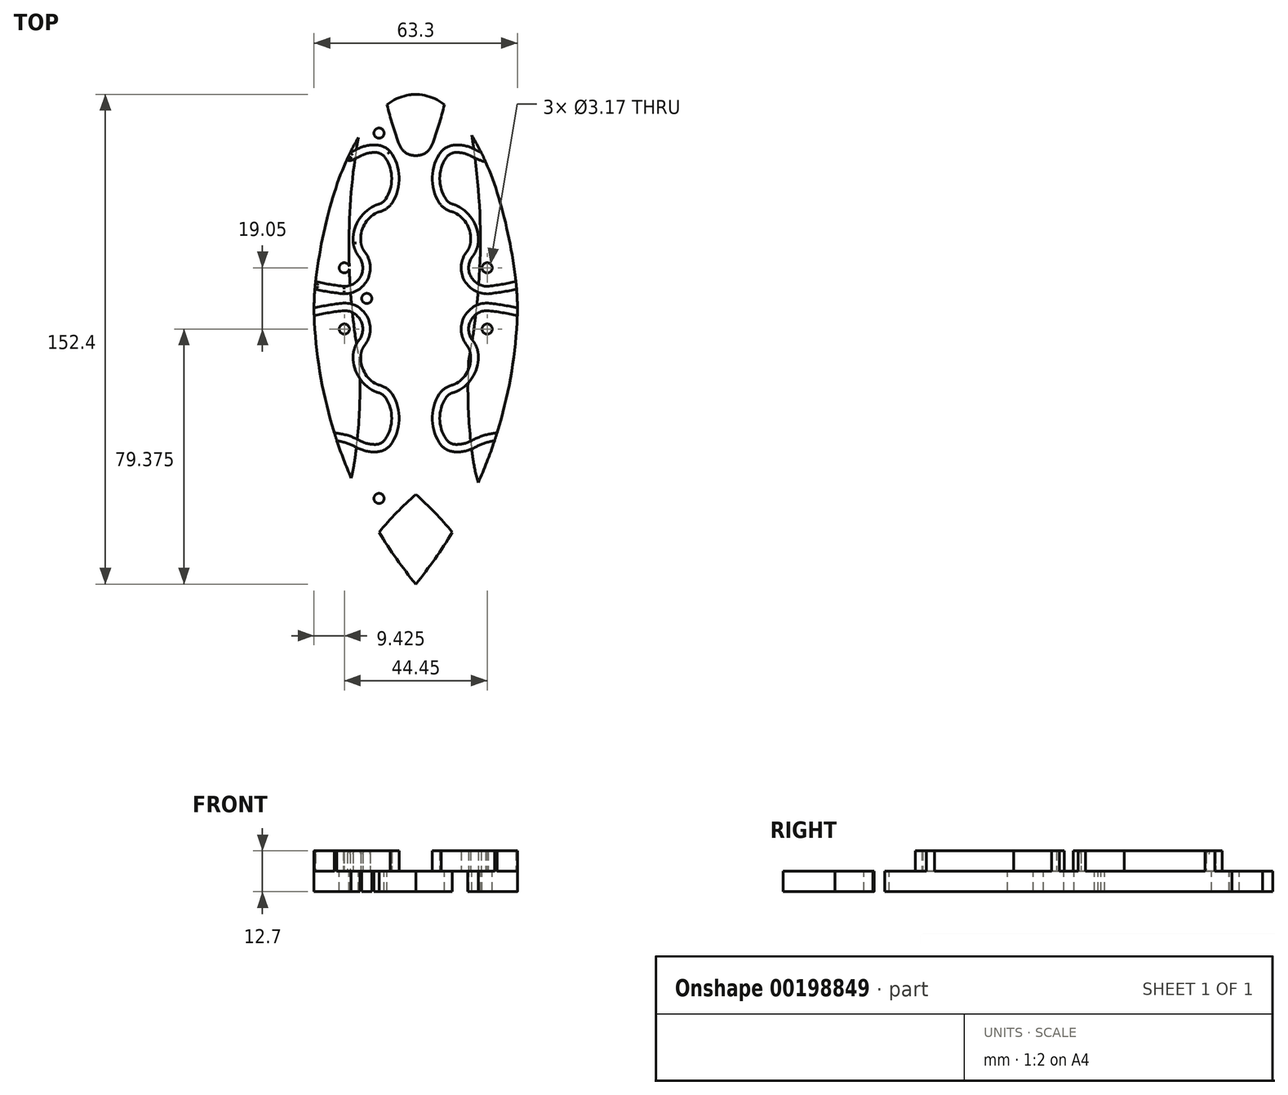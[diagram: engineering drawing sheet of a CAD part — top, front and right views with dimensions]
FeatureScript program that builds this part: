
annotation { "Feature Type Name" : "Feature", "Feature Type Description" : "" }
export const myFeature = defineFeature(function(context is Context, id is Id, definition is map)
    precondition{}
    {
        {
            var Q0;
            Q0=qCreatedBy(makeId("Top.planeOp"),FACE);
            var sketch = newSketch(context, id + "F0", { "sketchPlane" : qUnion([Q0])});
            skLineSegment(sketch, "E0", {"start": v(0, 0) * mm, "end": v(0, 80.69) * mm, "construction": true});
            skLineSegment(sketch, "E1", {"start": v(-64.8, 0) * mm, "end": v(76.72, 0) * mm, "construction": true});
            skLineSegment(sketch, "E2", {"start": v(0, 0) * mm, "end": v(0, -115.81) * mm, "construction": true});
            skPoint(sketch, "E3", {"position": v(0, 63.5) * mm});
            skPoint(sketch, "E4", {"position": v(31.75, 0) * mm});
            skPoint(sketch, "E5", {"position": v(-31.75, 0) * mm});
            skPoint(sketch, "E6", {"position": v(0, -88.9) * mm});
            skPoint(sketch, "E7", {"position": v(0, -19.05) * mm});
            skEllipticalArc(sketch, "E8", {});
            skPoint(sketch, "E9", {"position": v(0, -63.5) * mm});
            skPoint(sketch, "E10", {"position": v(16.51, -63.5) * mm});
            skArc(sketch, "E11", {"start": v(0, -88.9) * mm, "mid": v(22.23, -50.65) * mm, "end": v(31.54, -7.4) * mm});
            skArc(sketch, "E12.MirrorCS", {"start": v(0, -88.9) * mm, "mid": v(-22.23, -50.65) * mm, "end": v(-31.54, -7.4) * mm});
            skArc(sketch, "E13.filletArc", {"start": v(-31.03, 6.47) * mm, "mid": v(-31.6, -0.45) * mm, "end": v(-31.54, -7.4) * mm});
            skArc(sketch, "E14.MirrorCS", {"start": v(31.03, 6.47) * mm, "mid": v(31.6, -0.45) * mm, "end": v(31.54, -7.4) * mm});
            skPoint(sketch, "E15", {"position": v(-19.05, 76.2) * mm});
            skPoint(sketch, "E16", {"position": v(19.05, 76.2) * mm});
            skArc(sketch, "E17", {"start": v(-19.05, 47.97) * mm, "mid": v(-17.86, 62.09) * mm, "end": v(-19.05, 76.2) * mm});
            skArc(sketch, "E18", {"start": v(-19.05, 76.2) * mm, "mid": v(-11.04, 67.58) * mm, "end": v(0, 63.5) * mm});
            skArc(sketch, "E19.MirrorCS", {"start": v(19.05, 47.97) * mm, "mid": v(17.86, 62.09) * mm, "end": v(19.05, 76.2) * mm});
            skArc(sketch, "E20.MirrorCS", {"start": v(19.05, 76.2) * mm, "mid": v(11.04, 67.58) * mm, "end": v(0, 63.5) * mm});
            const initialGuessF0  = {"E8": [0, -0.01905, 0, 1, 0.08255, 0.03263075260586246, 5.026736623577707, 1.2564486836018787]};
            skSetInitialGuess(sketch, initialGuessF0);
            skSolve(sketch);
        }
        {
            var Q0;
            Q0=makeQuery(id+"F0.imprint","IMPRINT",FACE,{"disambiguationData":[TD([[makeQuery(id+"F0.imprint","IMPRINT",EDGE,{"derivedFrom":sQuery(id+"F0.wireOp",EDGE,"E8")}),1.0]])]});
            extrude(context, id + "F1", {"entities" : qUnion([Q0]), "oppositeDirection" : true, "depth" : 6.35 * mm});
        }
        {
            var Q0;
            Q0=qCreatedBy(makeId("Top.planeOp"),FACE);
            var sketch = newSketch(context, id + "F2", { "sketchPlane" : qUnion([Q0])});
            skLineSegment(sketch, "E21", {"start": v(0, -123.95) * mm, "end": v(0, 157.96) * mm, "construction": true});
            skLineSegment(sketch, "E22", {"start": v(104.8, 0) * mm, "end": v(-112.4, 0) * mm, "construction": true});
            skPoint(sketch, "E23", {"position": v(22.23, 0) * mm});
            skPoint(sketch, "E24", {"position": v(22.23, 9.52) * mm});
            skPoint(sketch, "E25", {"position": v(12.7, 0) * mm});
            skPoint(sketch, "E26", {"position": v(12.7, 41.27) * mm});
            skPoint(sketch, "E27", {"position": v(12.7, 33.34) * mm});
            skPoint(sketch, "E28", {"position": v(22.23, -15.88) * mm});
            skPoint(sketch, "E29", {"position": v(19.05, 0) * mm});
            skPoint(sketch, "E30", {"position": v(19.05, -31.46) * mm});
            skPoint(sketch, "E31", {"position": v(19.05, -39.84) * mm});
            skSolve(sketch);
        }
        {
            var Q0;
            Q0=qCreatedBy(makeId("Top.planeOp"),FACE);
            var sketch = newSketch(context, id + "F3", { "sketchPlane" : qUnion([Q0])});
            skPoint(sketch, "E32", {"position": v(76.2, 76.2) * mm});
            skLineSegment(sketch, "E33", {"start": v(-207.32, 0) * mm, "end": v(117.03, 0) * mm, "construction": true});
            skLineSegment(sketch, "E34", {"start": v(0, 0) * mm, "end": v(0, 84.75) * mm, "construction": true});
            skPoint(sketch, "E35", {"position": v(22.22, 9.52) * mm});
            skPoint(sketch, "E36", {"position": v(12.7, 33.34) * mm});
            skPoint(sketch, "E37", {"position": v(12.7, 41.28) * mm});
            skCircle(sketch, "E38", {"center": v(76.2, 76.2) * mm, "radius": 11.11 * mm});
            skArc(sketch, "E39", {"start": v(64.87, 81.94) * mm, "mid": v(76.2, 63.5) * mm, "end": v(87.53, 81.94) * mm});
            skCircle(sketch, "E40", {"center": v(76.2, 76.2) * mm, "radius": 15.88 * mm, "construction": true});
            skArc(sketch, "E41", {"start": v(21.55, 15.04) * mm, "mid": v(16.68, 9.19) * mm, "end": v(22.22, 3.97) * mm});
            skPoint(sketch, "E42", {"position": v(12.7, 27.37) * mm});
            skPoint(sketch, "E43", {"position": v(63.5, 76.2) * mm});
            skPoint(sketch, "E44", {"position": v(88.9, 76.2) * mm});
            skPoint(sketch, "E45", {"position": v(61.91, 63.5) * mm});
            skPoint(sketch, "E46", {"position": v(50.8, 46.04) * mm});
            skPoint(sketch, "E47", {"position": v(31.75, 41.28) * mm});
            skPoint(sketch, "E48", {"position": v(19.05, 42.86) * mm});
            skArc(sketch, "E49", {"start": v(50.8, 46.04) * mm, "mid": v(60.54, 59.7) * mm, "end": v(63.5, 76.2) * mm});
            skArc(sketch, "E50", {"start": v(23.54, 41.87) * mm, "mid": v(37.5, 41.77) * mm, "end": v(50.8, 46.04) * mm});
            skPoint(sketch, "E51", {"position": v(76.2, 127) * mm});
            skLineSegment(sketch, "E52", {"start": v(76.2, 76.2) * mm, "end": v(76.2, 127) * mm, "construction": true});
            skArc(sketch, "E53", {"start": v(77.79, 125.41) * mm, "mid": v(76.2, 127) * mm, "end": v(74.61, 125.41) * mm});
            skPoint(sketch, "E54", {"position": v(77.79, 125.41) * mm});
            skPoint(sketch, "E55", {"position": v(74.61, 125.41) * mm});
            skPoint(sketch, "E56", {"position": v(65.2, 82.55) * mm});
            skLineSegment(sketch, "E57", {"start": v(63.5, 76.2) * mm, "end": v(88.9, 76.2) * mm, "construction": true});
            skPoint(sketch, "E58", {"position": v(87.2, 82.55) * mm});
            skArc(sketch, "E59", {"start": v(77.79, 125.41) * mm, "mid": v(80.38, 104.21) * mm, "end": v(86.68, 83.8) * mm});
            skArc(sketch, "E60", {"start": v(65.72, 83.8) * mm, "mid": v(72.02, 104.21) * mm, "end": v(74.61, 125.41) * mm});
            skArc(sketch, "E61.filletArc", {"start": v(64.87, 81.94) * mm, "mid": v(65.31, 82.86) * mm, "end": v(65.72, 83.8) * mm});
            skArc(sketch, "E62.filletArc", {"start": v(86.68, 83.8) * mm, "mid": v(87.09, 82.86) * mm, "end": v(87.53, 81.94) * mm});
            skArc(sketch, "E63", {"start": v(87.53, 81.94) * mm, "mid": v(76.2, 88.9) * mm, "end": v(64.87, 81.94) * mm});
            skArc(sketch, "E64.0", {"start": v(80.56, 91.46) * mm, "mid": v(76.36, 92.07) * mm, "end": v(72.16, 91.55) * mm});
            skArc(sketch, "E65", {"start": v(76.52, 107.95) * mm, "mid": v(76.2, 108.27) * mm, "end": v(75.88, 107.95) * mm});
            skPoint(sketch, "E66", {"position": v(75.88, 107.95) * mm});
            skPoint(sketch, "E67", {"position": v(76.52, 107.95) * mm});
            skArc(sketch, "E68", {"start": v(72.16, 91.55) * mm, "mid": v(74.3, 99.69) * mm, "end": v(75.88, 107.95) * mm});
            skArc(sketch, "E69", {"start": v(76.52, 107.95) * mm, "mid": v(78.26, 99.64) * mm, "end": v(80.56, 91.46) * mm});
            skPoint(sketch, "E70", {"position": v(22.22, 3.97) * mm});
            skPoint(sketch, "E71", {"position": v(16.67, 9.52) * mm});
            skPoint(sketch, "E72", {"position": v(22.22, 15.08) * mm});
            skPoint(sketch, "E73", {"position": v(57.54, 53.98) * mm});
            skCircle(sketch, "E74", {"center": v(67.48, 46.06) * mm, "radius": 12.7 * mm, "construction": true});
            skLineSegment(sketch, "E75.bottom", {"start": v(57.54, 53.98) * mm, "end": v(77.4, 53.98) * mm, "construction": true});
            skLineSegment(sketch, "E75.top", {"start": v(57.54, 38.15) * mm, "end": v(77.4, 38.15) * mm, "construction": true});
            skLineSegment(sketch, "E75.left", {"start": v(57.54, 53.98) * mm, "end": v(57.54, 38.15) * mm, "construction": true});
            skLineSegment(sketch, "E75.right", {"start": v(77.4, 53.97) * mm, "end": v(77.4, 38.15) * mm, "construction": true});
            skArc(sketch, "E76", {"start": v(22.22, 3.97) * mm, "mid": v(69.22, 27.48) * mm, "end": v(88.9, 76.2) * mm});
            skCircle(sketch, "E77", {"center": v(12.7, 33.34) * mm, "radius": 3.97 * mm, "construction": true});
            skPoint(sketch, "E78", {"position": v(12.7, 45.24) * mm});
            skPoint(sketch, "E79", {"position": v(8.73, 41.28) * mm});
            skLineSegment(sketch, "E80.bottom", {"start": v(8.73, 41.28) * mm, "end": v(12.7, 41.28) * mm, "construction": true});
            skLineSegment(sketch, "E80.top", {"start": v(8.73, 45.24) * mm, "end": v(12.7, 45.24) * mm, "construction": true});
            skLineSegment(sketch, "E80.left", {"start": v(8.73, 41.28) * mm, "end": v(8.73, 45.24) * mm, "construction": true});
            skLineSegment(sketch, "E80.right", {"start": v(12.7, 41.28) * mm, "end": v(12.7, 45.24) * mm, "construction": true});
            skLineSegment(sketch, "E81", {"start": v(12.7, 41.27) * mm, "end": v(8.73, 45.24) * mm, "construction": true});
            skPoint(sketch, "E82", {"position": v(9.9, 44.08) * mm});
            skPoint(sketch, "E83", {"position": v(12.7, 37.3) * mm});
            skLineSegment(sketch, "E84", {"start": v(12.7, 37.3) * mm, "end": v(0, 37.3) * mm, "construction": true});
            skPoint(sketch, "E85.MirrorP", {"position": v(9.9, 30.53) * mm});
            skArc(sketch, "E86", {"start": v(9.9, 44.08) * mm, "mid": v(7.67, 37.3) * mm, "end": v(9.9, 30.53) * mm});
            skArc(sketch, "E87", {"start": v(12.7, 45.24) * mm, "mid": v(11.18, 44.94) * mm, "end": v(9.9, 44.08) * mm});
            skArc(sketch, "E88.MirrorCS", {"start": v(12.09, 29.42) * mm, "mid": v(10.9, 29.8) * mm, "end": v(9.9, 30.53) * mm});
            skArc(sketch, "E89", {"start": v(17.4, 44.02) * mm, "mid": v(15.13, 44.93) * mm, "end": v(12.7, 45.24) * mm});
            skArc(sketch, "E90.filletArc", {"start": v(17.4, 44.02) * mm, "mid": v(20.38, 42.68) * mm, "end": v(23.54, 41.87) * mm});
            skLineSegment(sketch, "E91", {"start": v(12.7, 37.3) * mm, "end": v(22.22, 9.52) * mm, "construction": true});
            skPoint(sketch, "E92", {"position": v(17.46, 23.42) * mm});
            skArc(sketch, "E93", {"start": v(17.46, 23.42) * mm, "mid": v(59, 36.27) * mm, "end": v(76.2, 76.2) * mm, "construction": true});
            skPoint(sketch, "E94", {"position": v(46.35, 27.89) * mm});
            skArc(sketch, "E95", {"start": v(23.97, 15.5) * mm, "mid": v(35.96, 20.26) * mm, "end": v(46.35, 27.89) * mm});
            skArc(sketch, "E96", {"start": v(13.98, 29.02) * mm, "mid": v(30.1, 26.65) * mm, "end": v(46.35, 27.89) * mm});
            skPoint(sketch, "E97.visualSharp", {"position": v(12.7, 29.37) * mm});
            skArc(sketch, "E97.filletArc", {"start": v(13.98, 29.02) * mm, "mid": v(13.04, 29.24) * mm, "end": v(12.09, 29.42) * mm});
            skArc(sketch, "E98.filletArc", {"start": v(21.55, 15.04) * mm, "mid": v(22.77, 15.23) * mm, "end": v(23.97, 15.5) * mm});
            skPoint(sketch, "E99", {"position": v(76.2, 92.08) * mm});
            skArc(sketch, "E100.MirrorCS", {"start": v(22.22, -3.97) * mm, "mid": v(69.22, -27.48) * mm, "end": v(88.9, -76.2) * mm});
            skArc(sketch, "E101.MirrorCS", {"start": v(21.55, -15.04) * mm, "mid": v(16.68, -9.19) * mm, "end": v(22.22, -3.97) * mm});
            skArc(sketch, "E102.MirrorCS", {"start": v(23.97, -15.5) * mm, "mid": v(35.96, -20.26) * mm, "end": v(46.35, -27.89) * mm});
            skArc(sketch, "E103.MirrorCS", {"start": v(13.98, -29.02) * mm, "mid": v(30.1, -26.65) * mm, "end": v(46.35, -27.89) * mm});
            skCircle(sketch, "E104.MirrorC", {"center": v(76.2, -76.2) * mm, "radius": 11.11 * mm});
            skArc(sketch, "E105.MirrorCS", {"start": v(64.87, -81.94) * mm, "mid": v(76.2, -63.5) * mm, "end": v(87.53, -81.94) * mm});
            skArc(sketch, "E106.MirrorCS", {"start": v(23.54, -41.87) * mm, "mid": v(37.5, -41.77) * mm, "end": v(50.8, -46.04) * mm});
            skArc(sketch, "E107.MirrorCS", {"start": v(77.79, -125.41) * mm, "mid": v(80.38, -104.21) * mm, "end": v(86.68, -83.8) * mm});
            skArc(sketch, "E108.MirrorCS", {"start": v(76.52, -107.95) * mm, "mid": v(78.26, -99.64) * mm, "end": v(80.56, -91.46) * mm});
            skArc(sketch, "E109.MirrorCS", {"start": v(72.16, -91.55) * mm, "mid": v(74.3, -99.69) * mm, "end": v(75.88, -107.95) * mm});
            skArc(sketch, "E110.MirrorCS", {"start": v(65.72, -83.8) * mm, "mid": v(72.02, -104.21) * mm, "end": v(74.61, -125.41) * mm});
            skArc(sketch, "E111.MirrorCS", {"start": v(80.56, -91.46) * mm, "mid": v(76.36, -92.07) * mm, "end": v(72.16, -91.55) * mm});
            skCircle(sketch, "E112.MirrorC", {"center": v(67.48, -46.06) * mm, "radius": 12.7 * mm, "construction": true});
            skArc(sketch, "E113.MirrorCS", {"start": v(50.8, -46.04) * mm, "mid": v(60.54, -59.7) * mm, "end": v(63.5, -76.2) * mm});
            skCircle(sketch, "E114.MirrorC", {"center": v(12.7, -33.34) * mm, "radius": 3.97 * mm, "construction": true});
            skCircle(sketch, "E115.MirrorC", {"center": v(12.7, -41.28) * mm, "radius": 3.97 * mm, "construction": true});
            skArc(sketch, "E116.MirrorCS", {"start": v(9.9, -44.08) * mm, "mid": v(7.67, -37.3) * mm, "end": v(9.9, -30.53) * mm});
            skArc(sketch, "E117.MirrorCS", {"start": v(13.98, -29.02) * mm, "mid": v(13.04, -29.24) * mm, "end": v(12.09, -29.42) * mm});
            skArc(sketch, "E118.MirrorCS", {"start": v(12.09, -29.42) * mm, "mid": v(10.9, -29.8) * mm, "end": v(9.9, -30.53) * mm});
            skArc(sketch, "E119.MirrorCS", {"start": v(17.4, -44.02) * mm, "mid": v(20.38, -42.68) * mm, "end": v(23.54, -41.87) * mm});
            skArc(sketch, "E120.MirrorCS", {"start": v(17.4, -44.02) * mm, "mid": v(15.13, -44.93) * mm, "end": v(12.7, -45.24) * mm});
            skArc(sketch, "E121.MirrorCS", {"start": v(21.55, -15.04) * mm, "mid": v(22.77, -15.23) * mm, "end": v(23.97, -15.5) * mm});
            skArc(sketch, "E122.0", {"start": v(13.33, 26.56) * mm, "mid": v(30.01, 24.11) * mm, "end": v(46.83, 25.4) * mm});
            skArc(sketch, "E122.1", {"start": v(13.33, 26.56) * mm, "mid": v(12.52, 26.76) * mm, "end": v(11.7, 26.9) * mm});
            skArc(sketch, "E122.2", {"start": v(18.64, 46.24) * mm, "mid": v(15.77, 47.4) * mm, "end": v(12.7, 47.78) * mm});
            skArc(sketch, "E122.3", {"start": v(12.7, 47.78) * mm, "mid": v(10.11, 47.25) * mm, "end": v(7.95, 45.73) * mm});
            skArc(sketch, "E122.4", {"start": v(7.95, 45.73) * mm, "mid": v(5.13, 37.3) * mm, "end": v(7.95, 28.88) * mm});
            skArc(sketch, "E122.5", {"start": v(11.7, 26.9) * mm, "mid": v(9.66, 27.58) * mm, "end": v(7.95, 28.88) * mm});
            skArc(sketch, "E123.0", {"start": v(18.64, 46.24) * mm, "mid": v(21.22, 45.08) * mm, "end": v(23.96, 44.37) * mm});
            skSolve(sketch);
        }
        {
            var Q0;
            Q0=qSketchRegion(id+"F3",true);
            var sketch = newSketch(context, id + "F4", { "sketchPlane" : qUnion([Q0])});
            skFitSpline(sketch, "E124.0", {"points": [v(0, 63.5) * mm, v(-8.65, 63.5) * mm, v(-16.95, 54.8) * mm, v(-29.2, 23.84) * mm, v(-32.63, 2.84) * mm, v(-32.63, -40.94) * mm, v(-29.2, -61.94) * mm, v(-16.95, -92.9) * mm, v(-8.65, -101.6) * mm, v(8.65, -101.6) * mm, v(16.95, -92.9) * mm, v(29.2, -61.94) * mm, v(32.63, -40.94) * mm, v(32.63, 2.84) * mm, v(29.2, 23.84) * mm, v(16.95, 54.8) * mm, v(8.65, 63.5) * mm, v(0, 63.5) * mm]});
            skArc(sketch, "E125.0", {"start": v(23.34, 17.96) * mm, "mid": v(26.1, 18.75) * mm, "end": v(28.8, 19.71) * mm});
            skArc(sketch, "E125.1", {"start": v(21.24, 17.56) * mm, "mid": v(22.3, 17.73) * mm, "end": v(23.34, 17.96) * mm});
            skArc(sketch, "E125.2", {"start": v(21.24, 17.56) * mm, "mid": v(14.15, 8.96) * mm, "end": v(22.37, 1.43) * mm});
            skArc(sketch, "E125.3", {"start": v(22.37, 1.43) * mm, "mid": v(26.9, 2.03) * mm, "end": v(31.4, 2.9) * mm});
            skArc(sketch, "E126.0", {"start": v(22.23, 3.78) * mm, "mid": v(26.73, 4.38) * mm, "end": v(31.18, 5.25) * mm});
            skArc(sketch, "E126.1", {"start": v(21.53, 15.23) * mm, "mid": v(16.49, 9.17) * mm, "end": v(22.23, 3.78) * mm});
            skArc(sketch, "E126.2", {"start": v(21.53, 15.23) * mm, "mid": v(22.73, 15.42) * mm, "end": v(23.93, 15.68) * mm});
            skArc(sketch, "E126.3", {"start": v(23.93, 15.68) * mm, "mid": v(26.63, 16.45) * mm, "end": v(29.28, 17.38) * mm});
            skFitSpline(sketch, "E127.0", {"points": [v(0, 63.5) * mm, v(-8.65, 63.5) * mm, v(-16.95, 54.8) * mm, v(-29.2, 23.84) * mm, v(-32.63, 2.84) * mm, v(-32.63, -40.94) * mm, v(-29.2, -61.94) * mm, v(-16.95, -92.9) * mm, v(-8.65, -101.6) * mm, v(8.65, -101.6) * mm, v(16.95, -92.9) * mm, v(29.2, -61.94) * mm, v(32.63, -40.94) * mm, v(32.63, 2.84) * mm, v(29.2, 23.84) * mm, v(16.95, 54.8) * mm, v(8.65, 63.5) * mm, v(0, 63.5) * mm]});
            skFitSpline(sketch, "E128.0", {"points": [v(0, 63.5) * mm, v(-8.65, 63.5) * mm, v(-16.95, 54.8) * mm, v(-29.2, 23.84) * mm, v(-32.63, 2.84) * mm, v(-32.63, -40.94) * mm, v(-29.2, -61.94) * mm, v(-16.95, -92.9) * mm, v(-8.65, -101.6) * mm, v(8.65, -101.6) * mm, v(16.95, -92.9) * mm, v(29.2, -61.94) * mm, v(32.63, -40.94) * mm, v(32.63, 2.84) * mm, v(29.2, 23.84) * mm, v(16.95, 54.8) * mm, v(8.65, 63.5) * mm, v(0, 63.5) * mm]});
            skLineSegment(sketch, "E129", {"start": v(27.18, 26.62) * mm, "end": v(27.79, 24.22) * mm});
            skArc(sketch, "E130.MirrorCS", {"start": v(-21.24, 17.56) * mm, "mid": v(-14.15, 8.96) * mm, "end": v(-22.37, 1.43) * mm});
            skArc(sketch, "E131.MirrorCS", {"start": v(-21.24, 17.56) * mm, "mid": v(-22.3, 17.73) * mm, "end": v(-23.34, 17.96) * mm});
            skArc(sketch, "E132.MirrorCS", {"start": v(-23.34, 17.96) * mm, "mid": v(-26.1, 18.75) * mm, "end": v(-28.8, 19.71) * mm});
            skArc(sketch, "E133.MirrorCS", {"start": v(-23.93, 15.68) * mm, "mid": v(-26.63, 16.45) * mm, "end": v(-29.28, 17.38) * mm});
            skArc(sketch, "E134.MirrorCS", {"start": v(-21.53, 15.23) * mm, "mid": v(-22.73, 15.42) * mm, "end": v(-23.93, 15.68) * mm});
            skArc(sketch, "E135.MirrorCS", {"start": v(-21.53, 15.23) * mm, "mid": v(-16.49, 9.17) * mm, "end": v(-22.23, 3.78) * mm});
            skArc(sketch, "E136.MirrorCS", {"start": v(-22.23, 3.78) * mm, "mid": v(-26.73, 4.38) * mm, "end": v(-31.18, 5.25) * mm});
            skArc(sketch, "E137.MirrorCS", {"start": v(-22.37, 1.43) * mm, "mid": v(-26.9, 2.03) * mm, "end": v(-31.4, 2.9) * mm});
            skArc(sketch, "E138.MirrorCS", {"start": v(-31.18, 5.25) * mm, "mid": v(-31.3, 4.07) * mm, "end": v(-31.4, 2.9) * mm});
            skArc(sketch, "E139.MirrorCS", {"start": v(21.24, -17.56) * mm, "mid": v(14.15, -8.96) * mm, "end": v(22.37, -1.43) * mm});
            skArc(sketch, "E140.MirrorCS", {"start": v(21.53, -15.23) * mm, "mid": v(16.49, -9.17) * mm, "end": v(22.23, -3.78) * mm});
            skArc(sketch, "E141.MirrorCS", {"start": v(21.24, -17.56) * mm, "mid": v(22.3, -17.73) * mm, "end": v(23.34, -17.96) * mm});
            skArc(sketch, "E142.MirrorCS", {"start": v(21.53, -15.23) * mm, "mid": v(22.73, -15.42) * mm, "end": v(23.93, -15.68) * mm});
            skPoint(sketch, "E143.MirrorCS.end.orphan", {"position": v(-28.8, -19.71) * mm});
            skPoint(sketch, "E143.MirrorCS.start.orphan", {"position": v(-23.34, -17.96) * mm});
            skPoint(sketch, "E144.MirrorCS.end.orphan", {"position": v(-29.28, -17.38) * mm});
            skPoint(sketch, "E144.MirrorCS.start.orphan", {"position": v(-23.93, -15.68) * mm});
            skPoint(sketch, "E145.MirrorCS.end.orphan", {"position": v(-31.18, -5.25) * mm});
            skPoint(sketch, "E145.MirrorCS.start.orphan", {"position": v(-22.23, -3.78) * mm});
            skPoint(sketch, "E146.MirrorCS.end.orphan", {"position": v(-31.4, -2.9) * mm});
            skPoint(sketch, "E146.MirrorCS.start.orphan", {"position": v(-22.37, -1.43) * mm});
            skPoint(sketch, "E147.MirrorCS.end.orphan", {"position": v(31.4, -2.9) * mm});
            skPoint(sketch, "E147.MirrorCS.start.orphan", {"position": v(31.18, -5.25) * mm});
            skArc(sketch, "E148.0", {"start": v(31.18, 5.25) * mm, "mid": v(31.3, 4.07) * mm, "end": v(31.4, 2.9) * mm});
            skArc(sketch, "E148.1", {"start": v(30.24, -20.3) * mm, "mid": v(30.41, -19.1) * mm, "end": v(30.57, -17.89) * mm});
            skPoint(sketch, "E149.MirrorCS.start.orphan", {"position": v(22.23, -3.78) * mm});
            skPoint(sketch, "E150.MirrorCS.start.orphan", {"position": v(22.37, -1.43) * mm});
            skPoint(sketch, "E151.MirrorCS.end.orphan", {"position": v(29.28, -17.38) * mm});
            skPoint(sketch, "E151.MirrorCS.start.orphan", {"position": v(23.93, -15.68) * mm});
            skPoint(sketch, "E152.MirrorCS.end.orphan", {"position": v(28.8, -19.71) * mm});
            skPoint(sketch, "E152.MirrorCS.start.orphan", {"position": v(23.34, -17.96) * mm});
            skArc(sketch, "E153.0", {"start": v(22.48, -1.44) * mm, "mid": v(27.1, -2.06) * mm, "end": v(31.65, -2.95) * mm});
            skArc(sketch, "E154.0", {"start": v(22.24, -3.78) * mm, "mid": v(26.96, -4.42) * mm, "end": v(31.62, -5.35) * mm});
            skArc(sketch, "E155.0", {"start": v(23.34, -17.96) * mm, "mid": v(26.83, -19) * mm, "end": v(30.24, -20.3) * mm});
            skArc(sketch, "E156.0", {"start": v(23.93, -15.68) * mm, "mid": v(27.29, -16.67) * mm, "end": v(30.57, -17.89) * mm});
            skArc(sketch, "E157.trimOffspring", {"start": v(31.65, -2.95) * mm, "mid": v(31.65, -4.15) * mm, "end": v(31.62, -5.35) * mm});
            skArc(sketch, "E158", {"start": v(22.48, -1.44) * mm, "mid": v(22.43, -1.43) * mm, "end": v(22.37, -1.43) * mm});
            skArc(sketch, "E159", {"start": v(22.24, -3.78) * mm, "mid": v(22.24, -3.78) * mm, "end": v(22.23, -3.78) * mm});
            skArc(sketch, "E160", {"start": v(-28.8, 19.71) * mm, "mid": v(-29.07, 18.55) * mm, "end": v(-29.28, 17.38) * mm});
            skArc(sketch, "E161.MirrorCS", {"start": v(-31.65, -2.95) * mm, "mid": v(-31.65, -4.15) * mm, "end": v(-31.62, -5.35) * mm});
            skArc(sketch, "E162.MirrorCS", {"start": v(-22.48, -1.44) * mm, "mid": v(-27.1, -2.06) * mm, "end": v(-31.65, -2.95) * mm});
            skArc(sketch, "E163.MirrorCS", {"start": v(-22.24, -3.78) * mm, "mid": v(-26.96, -4.42) * mm, "end": v(-31.62, -5.35) * mm});
            skArc(sketch, "E164.MirrorCS", {"start": v(-21.53, -15.23) * mm, "mid": v(-16.49, -9.17) * mm, "end": v(-22.23, -3.78) * mm});
            skArc(sketch, "E165.MirrorCS", {"start": v(-21.24, -17.56) * mm, "mid": v(-14.15, -8.96) * mm, "end": v(-22.37, -1.43) * mm});
            skArc(sketch, "E166.MirrorCS", {"start": v(-22.48, -1.44) * mm, "mid": v(-22.43, -1.43) * mm, "end": v(-22.37, -1.43) * mm});
            skArc(sketch, "E167.MirrorCS", {"start": v(-22.24, -3.78) * mm, "mid": v(-22.24, -3.78) * mm, "end": v(-22.23, -3.78) * mm});
            skArc(sketch, "E168.MirrorCS", {"start": v(-21.53, -15.23) * mm, "mid": v(-22.73, -15.42) * mm, "end": v(-23.93, -15.68) * mm});
            skArc(sketch, "E169.MirrorCS", {"start": v(-21.24, -17.56) * mm, "mid": v(-22.3, -17.73) * mm, "end": v(-23.34, -17.96) * mm});
            skArc(sketch, "E170.MirrorCS", {"start": v(-23.34, -17.96) * mm, "mid": v(-26.83, -19) * mm, "end": v(-30.24, -20.3) * mm});
            skArc(sketch, "E171.MirrorCS", {"start": v(-23.93, -15.68) * mm, "mid": v(-27.29, -16.67) * mm, "end": v(-30.57, -17.89) * mm});
            skArc(sketch, "E172.MirrorCS", {"start": v(-30.24, -20.3) * mm, "mid": v(-30.41, -19.1) * mm, "end": v(-30.57, -17.89) * mm});
            skLineSegment(sketch, "E173", {"start": v(-51.74, 0) * mm, "end": v(55.96, 0) * mm, "construction": true});
            skLineSegment(sketch, "E174", {"start": v(0, 72.52) * mm, "end": v(0, -77) * mm, "construction": true});
            skSolve(sketch);
        }
        {
            var Q0;
            Q0=qCreatedBy(makeId("Top.planeOp"),FACE);
            var sketch = newSketch(context, id + "F5", { "sketchPlane" : qUnion([Q0])});
            skArc(sketch, "E175", {"start": v(21.77, 42.45) * mm, "mid": v(21.1, 43.93) * mm, "end": v(20.4, 45.4) * mm});
            skArc(sketch, "E176", {"start": v(27.79, 24.22) * mm, "mid": v(27.51, 25.43) * mm, "end": v(27.18, 26.62) * mm});
            skArc(sketch, "E177.0", {"start": v(17.5, 44.19) * mm, "mid": v(19.58, 43.19) * mm, "end": v(21.77, 42.45) * mm});
            skArc(sketch, "E177.1", {"start": v(13.93, 28.84) * mm, "mid": v(20.5, 27.43) * mm, "end": v(27.18, 26.62) * mm});
            skArc(sketch, "E177.2", {"start": v(13.93, 28.84) * mm, "mid": v(12.97, 29.06) * mm, "end": v(12, 29.24) * mm});
            skArc(sketch, "E177.3", {"start": v(9.42, 43.73) * mm, "mid": v(7.48, 37.32) * mm, "end": v(9.4, 30.9) * mm});
            skArc(sketch, "E177.4", {"start": v(17.5, 44.19) * mm, "mid": v(15.1, 45.14) * mm, "end": v(12.52, 45.43) * mm});
            skPoint(sketch, "E178.visualSharp", {"position": v(10.58, 29.4) * mm});
            skArc(sketch, "E178.filletArc", {"start": v(9.4, 30.9) * mm, "mid": v(10.53, 29.8) * mm, "end": v(12, 29.24) * mm});
            skPoint(sketch, "E179.visualSharp", {"position": v(10.57, 45.2) * mm});
            skArc(sketch, "E179.filletArc", {"start": v(12.52, 45.43) * mm, "mid": v(10.76, 44.96) * mm, "end": v(9.42, 43.73) * mm});
            skArc(sketch, "E180.0", {"start": v(18.64, 46.24) * mm, "mid": v(19.5, 45.8) * mm, "end": v(20.4, 45.4) * mm});
            skArc(sketch, "E180.1", {"start": v(18.64, 46.24) * mm, "mid": v(15.77, 47.4) * mm, "end": v(12.7, 47.78) * mm});
            skArc(sketch, "E180.2", {"start": v(12.7, 47.78) * mm, "mid": v(10.11, 47.25) * mm, "end": v(7.95, 45.73) * mm});
            skArc(sketch, "E180.3", {"start": v(13.33, 26.56) * mm, "mid": v(20.5, 25.05) * mm, "end": v(27.79, 24.22) * mm});
            skArc(sketch, "E180.4", {"start": v(13.33, 26.56) * mm, "mid": v(12.52, 26.76) * mm, "end": v(11.7, 26.9) * mm});
            skArc(sketch, "E180.5", {"start": v(11.7, 26.9) * mm, "mid": v(9.66, 27.58) * mm, "end": v(7.95, 28.88) * mm});
            skArc(sketch, "E180.6", {"start": v(7.95, 45.73) * mm, "mid": v(5.13, 37.3) * mm, "end": v(7.95, 28.88) * mm});
            skArc(sketch, "E181.MirrorCS", {"start": v(-7.95, 45.73) * mm, "mid": v(-5.13, 37.3) * mm, "end": v(-7.95, 28.88) * mm});
            skArc(sketch, "E182.MirrorCS", {"start": v(-12.7, 47.78) * mm, "mid": v(-10.11, 47.25) * mm, "end": v(-7.95, 45.73) * mm});
            skArc(sketch, "E183.MirrorCS", {"start": v(-18.64, 46.24) * mm, "mid": v(-15.77, 47.4) * mm, "end": v(-12.7, 47.78) * mm});
            skArc(sketch, "E184.MirrorCS", {"start": v(-12.52, 45.43) * mm, "mid": v(-10.76, 44.96) * mm, "end": v(-9.42, 43.73) * mm});
            skArc(sketch, "E185.MirrorCS", {"start": v(-9.42, 43.73) * mm, "mid": v(-7.48, 37.32) * mm, "end": v(-9.4, 30.9) * mm});
            skArc(sketch, "E186.MirrorCS", {"start": v(-9.4, 30.9) * mm, "mid": v(-10.53, 29.8) * mm, "end": v(-12, 29.24) * mm});
            skArc(sketch, "E187.MirrorCS", {"start": v(-11.7, 26.9) * mm, "mid": v(-9.66, 27.58) * mm, "end": v(-7.95, 28.88) * mm});
            skArc(sketch, "E188.MirrorCS", {"start": v(-13.33, 26.56) * mm, "mid": v(-12.52, 26.76) * mm, "end": v(-11.7, 26.9) * mm});
            skArc(sketch, "E189.MirrorCS", {"start": v(-13.93, 28.84) * mm, "mid": v(-12.97, 29.06) * mm, "end": v(-12, 29.24) * mm});
            skArc(sketch, "E190.MirrorCS", {"start": v(-13.93, 28.84) * mm, "mid": v(-20.5, 27.43) * mm, "end": v(-27.18, 26.62) * mm});
            skArc(sketch, "E191.MirrorCS", {"start": v(-13.33, 26.56) * mm, "mid": v(-20.5, 25.05) * mm, "end": v(-27.79, 24.22) * mm});
            skArc(sketch, "E192.MirrorCS", {"start": v(-17.5, 44.19) * mm, "mid": v(-19.58, 43.19) * mm, "end": v(-21.77, 42.45) * mm});
            skArc(sketch, "E193.MirrorCS", {"start": v(-17.5, 44.19) * mm, "mid": v(-15.1, 45.14) * mm, "end": v(-12.52, 45.43) * mm});
            skArc(sketch, "E194.MirrorCS", {"start": v(-18.64, 46.24) * mm, "mid": v(-19.5, 45.8) * mm, "end": v(-20.4, 45.4) * mm});
            skArc(sketch, "E195.MirrorCS", {"start": v(-21.77, 42.45) * mm, "mid": v(-21.1, 43.93) * mm, "end": v(-20.4, 45.4) * mm});
            skArc(sketch, "E196.MirrorCS", {"start": v(-27.79, 24.22) * mm, "mid": v(-27.51, 25.43) * mm, "end": v(-27.18, 26.62) * mm});
            skArc(sketch, "E197.MirrorCS", {"start": v(13.33, -26.56) * mm, "mid": v(12.52, -26.76) * mm, "end": v(11.7, -26.9) * mm});
            skArc(sketch, "E198.MirrorCS", {"start": v(11.7, -26.9) * mm, "mid": v(9.66, -27.58) * mm, "end": v(7.95, -28.88) * mm});
            skArc(sketch, "E199.MirrorCS", {"start": v(7.95, -45.73) * mm, "mid": v(5.13, -37.3) * mm, "end": v(7.95, -28.88) * mm});
            skArc(sketch, "E200.MirrorCS", {"start": v(12.7, -47.78) * mm, "mid": v(10.11, -47.25) * mm, "end": v(7.95, -45.73) * mm});
            skArc(sketch, "E201.MirrorCS", {"start": v(9.42, -43.73) * mm, "mid": v(7.48, -37.32) * mm, "end": v(9.4, -30.9) * mm});
            skArc(sketch, "E202.MirrorCS", {"start": v(9.4, -30.9) * mm, "mid": v(10.53, -29.8) * mm, "end": v(12, -29.24) * mm});
            skArc(sketch, "E203.MirrorCS", {"start": v(13.93, -28.84) * mm, "mid": v(12.97, -29.06) * mm, "end": v(12, -29.24) * mm});
            skArc(sketch, "E204.MirrorCS", {"start": v(17.5, -44.19) * mm, "mid": v(15.1, -45.14) * mm, "end": v(12.52, -45.43) * mm});
            skArc(sketch, "E205.MirrorCS", {"start": v(12.52, -45.43) * mm, "mid": v(10.76, -44.96) * mm, "end": v(9.42, -43.73) * mm});
            skArc(sketch, "E206.MirrorCS", {"start": v(18.64, -46.24) * mm, "mid": v(15.77, -47.4) * mm, "end": v(12.7, -47.78) * mm});
            skArc(sketch, "E207.0", {"start": v(24.52, -44.28) * mm, "mid": v(24.93, -43.04) * mm, "end": v(25.32, -41.8) * mm});
            skPoint(sketch, "E208.MirrorCS.end.orphan", {"position": v(27.18, -26.62) * mm});
            skPoint(sketch, "E208.MirrorCS.start.orphan", {"position": v(13.93, -28.84) * mm});
            skPoint(sketch, "E209.MirrorCS.end.orphan", {"position": v(27.79, -24.22) * mm});
            skPoint(sketch, "E209.MirrorCS.start.orphan", {"position": v(13.33, -26.56) * mm});
            skPoint(sketch, "E210.MirrorCS.end.orphan", {"position": v(21.77, -42.45) * mm});
            skPoint(sketch, "E210.MirrorCS.start.orphan", {"position": v(17.5, -44.19) * mm});
            skPoint(sketch, "E211.MirrorCS.end.orphan", {"position": v(20.4, -45.4) * mm});
            skPoint(sketch, "E211.MirrorCS.start.orphan", {"position": v(18.64, -46.24) * mm});
            skArc(sketch, "E212.0", {"start": v(13.33, -26.56) * mm, "mid": v(21.4, -24.9) * mm, "end": v(29.62, -24.13) * mm});
            skArc(sketch, "E213.0", {"start": v(13.93, -28.84) * mm, "mid": v(21.5, -27.27) * mm, "end": v(29.18, -26.5) * mm});
            skArc(sketch, "E214.0", {"start": v(23.96, -44.37) * mm, "mid": v(24.24, -44.33) * mm, "end": v(24.52, -44.28) * mm});
            skArc(sketch, "E214.1", {"start": v(18.64, -46.24) * mm, "mid": v(21.22, -45.08) * mm, "end": v(23.96, -44.37) * mm});
            skArc(sketch, "E215.0", {"start": v(23.57, -42.06) * mm, "mid": v(24.45, -41.92) * mm, "end": v(25.32, -41.8) * mm});
            skArc(sketch, "E215.1", {"start": v(17.5, -44.19) * mm, "mid": v(20.44, -42.86) * mm, "end": v(23.57, -42.06) * mm});
            skArc(sketch, "E216.trimOffspring", {"start": v(29.18, -26.5) * mm, "mid": v(29.4, -25.31) * mm, "end": v(29.62, -24.13) * mm});
            skArc(sketch, "E217.MirrorCS", {"start": v(-23.57, -42.06) * mm, "mid": v(-24.45, -41.92) * mm, "end": v(-25.32, -41.8) * mm});
            skArc(sketch, "E218.MirrorCS", {"start": v(-23.96, -44.37) * mm, "mid": v(-24.24, -44.33) * mm, "end": v(-24.52, -44.28) * mm});
            skArc(sketch, "E219.MirrorCS", {"start": v(-13.33, -26.56) * mm, "mid": v(-12.52, -26.76) * mm, "end": v(-11.7, -26.9) * mm});
            skPoint(sketch, "E220.MirrorP", {"position": v(-21.77, -42.45) * mm});
            skArc(sketch, "E221.MirrorCS", {"start": v(-13.93, -28.84) * mm, "mid": v(-12.97, -29.06) * mm, "end": v(-12, -29.24) * mm});
            skArc(sketch, "E222.MirrorCS", {"start": v(-17.5, -44.19) * mm, "mid": v(-20.44, -42.86) * mm, "end": v(-23.57, -42.06) * mm});
            skArc(sketch, "E223.MirrorCS", {"start": v(-18.64, -46.24) * mm, "mid": v(-15.77, -47.4) * mm, "end": v(-12.7, -47.78) * mm});
            skArc(sketch, "E224.MirrorCS", {"start": v(-11.7, -26.9) * mm, "mid": v(-9.66, -27.58) * mm, "end": v(-7.95, -28.88) * mm});
            skPoint(sketch, "E225.MirrorP", {"position": v(-17.5, -44.19) * mm});
            skArc(sketch, "E226.MirrorCS", {"start": v(-18.64, -46.24) * mm, "mid": v(-21.22, -45.08) * mm, "end": v(-23.96, -44.37) * mm});
            skPoint(sketch, "E227.MirrorP", {"position": v(-20.4, -45.4) * mm});
            skArc(sketch, "E228.MirrorCS", {"start": v(-7.95, -45.73) * mm, "mid": v(-5.13, -37.3) * mm, "end": v(-7.95, -28.88) * mm});
            skPoint(sketch, "E229.MirrorP", {"position": v(-27.79, -24.22) * mm});
            skArc(sketch, "E230.MirrorCS", {"start": v(-12.52, -45.43) * mm, "mid": v(-10.76, -44.96) * mm, "end": v(-9.42, -43.73) * mm});
            skArc(sketch, "E231.MirrorCS", {"start": v(-17.5, -44.19) * mm, "mid": v(-15.1, -45.14) * mm, "end": v(-12.52, -45.43) * mm});
            skPoint(sketch, "E232.MirrorP", {"position": v(-18.64, -46.24) * mm});
            skArc(sketch, "E233.MirrorCS", {"start": v(-9.4, -30.9) * mm, "mid": v(-10.53, -29.8) * mm, "end": v(-12, -29.24) * mm});
            skArc(sketch, "E234.MirrorCS", {"start": v(-12.7, -47.78) * mm, "mid": v(-10.11, -47.25) * mm, "end": v(-7.95, -45.73) * mm});
            skArc(sketch, "E235.MirrorCS", {"start": v(-13.93, -28.84) * mm, "mid": v(-21.5, -27.27) * mm, "end": v(-29.18, -26.5) * mm});
            skArc(sketch, "E236.MirrorCS", {"start": v(-24.52, -44.28) * mm, "mid": v(-24.93, -43.04) * mm, "end": v(-25.32, -41.8) * mm});
            skArc(sketch, "E237.MirrorCS", {"start": v(-13.33, -26.56) * mm, "mid": v(-21.4, -24.9) * mm, "end": v(-29.62, -24.13) * mm});
            skPoint(sketch, "E238.MirrorP", {"position": v(-13.33, -26.56) * mm});
            skPoint(sketch, "E239.MirrorP", {"position": v(-27.18, -26.62) * mm});
            skArc(sketch, "E240.MirrorCS", {"start": v(-9.42, -43.73) * mm, "mid": v(-7.48, -37.32) * mm, "end": v(-9.4, -30.9) * mm});
            skPoint(sketch, "E241.MirrorP", {"position": v(-13.93, -28.84) * mm});
            skArc(sketch, "E242.MirrorCS", {"start": v(-29.18, -26.5) * mm, "mid": v(-29.4, -25.31) * mm, "end": v(-29.62, -24.13) * mm});
            skLineSegment(sketch, "E243", {"start": v(-65.43, 0) * mm, "end": v(71.76, 0) * mm, "construction": true});
            skLineSegment(sketch, "E244", {"start": v(0, 78.2) * mm, "end": v(0, -66.26) * mm, "construction": true});
            skPoint(sketch, "E245", {"position": v(0, 0) * mm});
            skSolve(sketch);
        }
        {
            var Q0;
            Q0=qCreatedBy(makeId("Top.planeOp"),FACE);
            var sketch = newSketch(context, id + "F6", { "sketchPlane" : qUnion([Q0])});
            skCircle(sketch, "E246", {"center": v(12.7, 41.27) * mm, "radius": 1.59 * mm});
            skCircle(sketch, "E247", {"center": v(12.7, 33.34) * mm, "radius": 1.59 * mm});
            skCircle(sketch, "E248", {"center": v(22.23, 9.52) * mm, "radius": 1.59 * mm});
            skCircle(sketch, "E249.MirrorC", {"center": v(-12.7, 41.27) * mm, "radius": 1.59 * mm});
            skCircle(sketch, "E250.MirrorC", {"center": v(-12.7, 33.34) * mm, "radius": 1.59 * mm});
            skCircle(sketch, "E251.MirrorC", {"center": v(-22.23, 9.52) * mm, "radius": 1.59 * mm});
            skCircle(sketch, "E252.MirrorC", {"center": v(-22.23, -9.52) * mm, "radius": 1.59 * mm});
            skCircle(sketch, "E253.MirrorC", {"center": v(-12.7, -33.34) * mm, "radius": 1.59 * mm});
            skCircle(sketch, "E254.MirrorC", {"center": v(-12.7, -41.27) * mm, "radius": 1.59 * mm});
            skCircle(sketch, "E255.MirrorC", {"center": v(22.23, -9.52) * mm, "radius": 1.59 * mm});
            skCircle(sketch, "E256.MirrorC", {"center": v(12.7, -41.27) * mm, "radius": 1.59 * mm});
            skCircle(sketch, "E257.MirrorC", {"center": v(12.7, -33.34) * mm, "radius": 1.59 * mm});
            skSolve(sketch);
        }
        {
            var Q0;
            Q0=qSketchRegion(id+"F6",true);
            extrude(context, id + "F7", {"entities" : qUnion([Q0]), "operationType" : NewBodyOperationType.REMOVE, "endBound" : BoundingType.THROUGH_ALL, "oppositeDirection" : true, "depth" : 25.4 * mm});
        }
        {
            var Q0;
            Q0=makeQuery(id+"F1.opExtrude","CAP_FACE",FACE,{"disambiguationData":[OSD([sQuery(id+"F0.wireOp",EDGE,"E8"),sQuery(id+"F0.wireOp",EDGE,"E11"),sQuery(id+"F0.wireOp",EDGE,"E12.MirrorCS"),sQuery(id+"F0.wireOp",EDGE,"E13.filletArc"),sQuery(id+"F0.wireOp",EDGE,"E14.MirrorCS")])],"isStart":false});
            cPlane(context, id + "F8", {"entities" : qUnion([Q0]), "cplaneType" : CPlaneType.OFFSET, "offset" : 0 * mm, "width" : 152.4 * mm, "height" : 152.4 * mm});
        }
        {
            var Q0;
            Q0=qCreatedBy(makeId("Top.planeOp"),FACE);
            var sketch = newSketch(context, id + "F9", { "sketchPlane" : qUnion([Q0])});
            skArc(sketch, "E258.0", {"start": v(18.64, 46.24) * mm, "mid": v(19.5, 45.8) * mm, "end": v(20.4, 45.4) * mm});
            skArc(sketch, "E258.1", {"start": v(18.64, 46.24) * mm, "mid": v(15.77, 47.4) * mm, "end": v(12.7, 47.78) * mm});
            skArc(sketch, "E258.4", {"start": v(7.95, 45.73) * mm, "mid": v(5.14, 37.83) * mm, "end": v(7.36, 29.74) * mm});
            skArc(sketch, "E258.5", {"start": v(12.7, 47.78) * mm, "mid": v(10.11, 47.25) * mm, "end": v(7.95, 45.73) * mm});
            skArc(sketch, "E259.2", {"start": v(9.4, 30.9) * mm, "mid": v(10.37, 29.9) * mm, "end": v(11.63, 29.31) * mm});
            skArc(sketch, "E260.0", {"start": v(9.42, 43.73) * mm, "mid": v(7.48, 37.32) * mm, "end": v(9.4, 30.9) * mm});
            skArc(sketch, "E260.1", {"start": v(12.52, 45.43) * mm, "mid": v(10.76, 44.96) * mm, "end": v(9.42, 43.73) * mm});
            skArc(sketch, "E260.2", {"start": v(17.5, 44.19) * mm, "mid": v(15.1, 45.14) * mm, "end": v(12.52, 45.43) * mm});
            skArc(sketch, "E260.3", {"start": v(17.5, 44.19) * mm, "mid": v(19.58, 43.19) * mm, "end": v(21.77, 42.45) * mm});
            skPoint(sketch, "E261.visualSharp", {"position": v(9.56, 27.1) * mm});
            skArc(sketch, "E261.filletArc", {"start": v(7.36, 29.74) * mm, "mid": v(9.02, 28) * mm, "end": v(11.21, 27) * mm});
            skArc(sketch, "E262.0", {"start": v(21.77, 42.45) * mm, "mid": v(21.1, 43.93) * mm, "end": v(20.4, 45.4) * mm});
            skArc(sketch, "E263.0", {"start": v(22.37, 1.43) * mm, "mid": v(26.9, 2.03) * mm, "end": v(31.4, 2.9) * mm});
            skArc(sketch, "E263.1", {"start": v(15.91, 14.6) * mm, "mid": v(14.96, 5.96) * mm, "end": v(22.37, 1.43) * mm});
            skArc(sketch, "E264.2", {"start": v(17.82, 13.22) * mm, "mid": v(17.02, 7.1) * mm, "end": v(22.23, 3.78) * mm});
            skArc(sketch, "E264.3", {"start": v(22.23, 3.78) * mm, "mid": v(26.73, 4.38) * mm, "end": v(31.18, 5.25) * mm});
            skArc(sketch, "E265.0", {"start": v(31.18, 5.25) * mm, "mid": v(31.3, 4.07) * mm, "end": v(31.4, 2.9) * mm});
            skArc(sketch, "E266", {"start": v(16.93, 16.78) * mm, "mid": v(16.3, 22.3) * mm, "end": v(12.6, 26.44) * mm});
            skArc(sketch, "E267.filletArc", {"start": v(15.91, 14.6) * mm, "mid": v(16.55, 15.63) * mm, "end": v(16.93, 16.78) * mm});
            skArc(sketch, "E268", {"start": v(19.44, 17.21) * mm, "mid": v(17.94, 24.06) * mm, "end": v(12.84, 28.86) * mm});
            skArc(sketch, "E269", {"start": v(18.26, 13.83) * mm, "mid": v(19.04, 15.46) * mm, "end": v(19.44, 17.21) * mm});
            skPoint(sketch, "E270.visualSharp", {"position": v(12, 29.24) * mm});
            skArc(sketch, "E270.filletArc", {"start": v(12.84, 28.86) * mm, "mid": v(12.25, 29.12) * mm, "end": v(11.63, 29.31) * mm});
            skArc(sketch, "E271.filletArc", {"start": v(17.82, 13.22) * mm, "mid": v(18.05, 13.52) * mm, "end": v(18.26, 13.83) * mm});
            skPoint(sketch, "E272.visualSharp", {"position": v(11.7, 26.9) * mm});
            skArc(sketch, "E272.filletArc", {"start": v(12.6, 26.44) * mm, "mid": v(11.93, 26.77) * mm, "end": v(11.21, 27) * mm});
            skArc(sketch, "E273.MirrorCS", {"start": v(-12.84, 28.86) * mm, "mid": v(-12.25, 29.12) * mm, "end": v(-11.63, 29.31) * mm});
            skArc(sketch, "E274.MirrorCS", {"start": v(-12.6, 26.44) * mm, "mid": v(-11.93, 26.77) * mm, "end": v(-11.21, 27) * mm});
            skArc(sketch, "E275.MirrorCS", {"start": v(-17.82, 13.22) * mm, "mid": v(-18.05, 13.52) * mm, "end": v(-18.26, 13.83) * mm});
            skArc(sketch, "E276.MirrorCS", {"start": v(-18.64, 46.24) * mm, "mid": v(-19.5, 45.8) * mm, "end": v(-20.4, 45.4) * mm});
            skArc(sketch, "E277.MirrorCS", {"start": v(-15.91, 14.6) * mm, "mid": v(-16.55, 15.63) * mm, "end": v(-16.93, 16.78) * mm});
            skArc(sketch, "E278.MirrorCS", {"start": v(-31.18, 5.25) * mm, "mid": v(-31.3, 4.07) * mm, "end": v(-31.4, 2.9) * mm});
            skArc(sketch, "E279.MirrorCS", {"start": v(-9.4, 30.9) * mm, "mid": v(-10.37, 29.9) * mm, "end": v(-11.63, 29.31) * mm});
            skArc(sketch, "E280.MirrorCS", {"start": v(-21.77, 42.45) * mm, "mid": v(-21.1, 43.93) * mm, "end": v(-20.4, 45.4) * mm});
            skArc(sketch, "E281.MirrorCS", {"start": v(-12.52, 45.43) * mm, "mid": v(-10.76, 44.96) * mm, "end": v(-9.42, 43.73) * mm});
            skArc(sketch, "E282.MirrorCS", {"start": v(-9.42, 43.73) * mm, "mid": v(-7.48, 37.32) * mm, "end": v(-9.4, 30.9) * mm});
            skArc(sketch, "E283.MirrorCS", {"start": v(-22.37, 1.43) * mm, "mid": v(-26.9, 2.03) * mm, "end": v(-31.4, 2.9) * mm});
            skArc(sketch, "E284.MirrorCS", {"start": v(-12.7, 47.78) * mm, "mid": v(-10.11, 47.25) * mm, "end": v(-7.95, 45.73) * mm});
            skArc(sketch, "E285.MirrorCS", {"start": v(-18.64, 46.24) * mm, "mid": v(-15.77, 47.4) * mm, "end": v(-12.7, 47.78) * mm});
            skPoint(sketch, "E286.MirrorP", {"position": v(-12, 29.24) * mm});
            skArc(sketch, "E287.MirrorCS", {"start": v(-16.93, 16.78) * mm, "mid": v(-16.3, 22.3) * mm, "end": v(-12.6, 26.44) * mm});
            skArc(sketch, "E288.MirrorCS", {"start": v(-7.36, 29.74) * mm, "mid": v(-9.02, 28) * mm, "end": v(-11.21, 27) * mm});
            skPoint(sketch, "E289.MirrorP", {"position": v(-9.56, 27.1) * mm});
            skPoint(sketch, "E290.MirrorP", {"position": v(-11.7, 26.9) * mm});
            skArc(sketch, "E291.MirrorCS", {"start": v(-18.26, 13.83) * mm, "mid": v(-19.04, 15.46) * mm, "end": v(-19.44, 17.21) * mm});
            skArc(sketch, "E292.MirrorCS", {"start": v(-19.44, 17.21) * mm, "mid": v(-17.94, 24.06) * mm, "end": v(-12.84, 28.86) * mm});
            skArc(sketch, "E293.MirrorCS", {"start": v(-17.5, 44.19) * mm, "mid": v(-15.1, 45.14) * mm, "end": v(-12.52, 45.43) * mm});
            skArc(sketch, "E294.MirrorCS", {"start": v(-17.82, 13.22) * mm, "mid": v(-17.02, 7.1) * mm, "end": v(-22.23, 3.78) * mm});
            skArc(sketch, "E295.MirrorCS", {"start": v(-15.91, 14.6) * mm, "mid": v(-14.96, 5.96) * mm, "end": v(-22.37, 1.43) * mm});
            skArc(sketch, "E296.MirrorCS", {"start": v(-17.5, 44.19) * mm, "mid": v(-19.58, 43.19) * mm, "end": v(-21.77, 42.45) * mm});
            skArc(sketch, "E297.MirrorCS", {"start": v(-7.95, 45.73) * mm, "mid": v(-5.14, 37.83) * mm, "end": v(-7.36, 29.74) * mm});
            skArc(sketch, "E298.MirrorCS", {"start": v(-22.23, 3.78) * mm, "mid": v(-26.73, 4.38) * mm, "end": v(-31.18, 5.25) * mm});
            skArc(sketch, "E299.MirrorCS", {"start": v(12.6, -26.44) * mm, "mid": v(11.93, -26.77) * mm, "end": v(11.21, -27) * mm});
            skArc(sketch, "E300.MirrorCS", {"start": v(12.84, -28.86) * mm, "mid": v(12.25, -29.12) * mm, "end": v(11.63, -29.31) * mm});
            skArc(sketch, "E301.MirrorCS", {"start": v(9.4, -30.9) * mm, "mid": v(10.37, -29.9) * mm, "end": v(11.63, -29.31) * mm});
            skArc(sketch, "E302.MirrorCS", {"start": v(15.91, -14.6) * mm, "mid": v(16.55, -15.63) * mm, "end": v(16.93, -16.78) * mm});
            skArc(sketch, "E303.MirrorCS", {"start": v(17.82, -13.22) * mm, "mid": v(18.05, -13.52) * mm, "end": v(18.26, -13.83) * mm});
            skArc(sketch, "E304.MirrorCS", {"start": v(12.52, -45.43) * mm, "mid": v(10.76, -44.96) * mm, "end": v(9.42, -43.73) * mm});
            skArc(sketch, "E305.MirrorCS", {"start": v(7.36, -29.74) * mm, "mid": v(9.02, -28) * mm, "end": v(11.21, -27) * mm});
            skArc(sketch, "E306.MirrorCS", {"start": v(18.26, -13.83) * mm, "mid": v(19.04, -15.46) * mm, "end": v(19.44, -17.21) * mm});
            skArc(sketch, "E307.MirrorCS", {"start": v(9.42, -43.73) * mm, "mid": v(7.48, -37.32) * mm, "end": v(9.4, -30.9) * mm});
            skArc(sketch, "E308.MirrorCS", {"start": v(15.91, -14.6) * mm, "mid": v(14.96, -5.96) * mm, "end": v(22.37, -1.43) * mm});
            skArc(sketch, "E309.MirrorCS", {"start": v(12.7, -47.78) * mm, "mid": v(10.11, -47.25) * mm, "end": v(7.95, -45.73) * mm});
            skArc(sketch, "E310.MirrorCS", {"start": v(7.95, -45.73) * mm, "mid": v(5.14, -37.83) * mm, "end": v(7.36, -29.74) * mm});
            skArc(sketch, "E311.MirrorCS", {"start": v(18.64, -46.24) * mm, "mid": v(15.77, -47.4) * mm, "end": v(12.7, -47.78) * mm});
            skPoint(sketch, "E312.MirrorP", {"position": v(11.7, -26.9) * mm});
            skArc(sketch, "E313.MirrorCS", {"start": v(19.44, -17.21) * mm, "mid": v(17.94, -24.06) * mm, "end": v(12.84, -28.86) * mm});
            skArc(sketch, "E314.MirrorCS", {"start": v(16.93, -16.78) * mm, "mid": v(16.3, -22.3) * mm, "end": v(12.6, -26.44) * mm});
            skArc(sketch, "E315.MirrorCS", {"start": v(17.82, -13.22) * mm, "mid": v(17.02, -7.1) * mm, "end": v(22.23, -3.78) * mm});
            skPoint(sketch, "E316.MirrorP", {"position": v(12, -29.24) * mm});
            skPoint(sketch, "E317.MirrorP", {"position": v(9.56, -27.1) * mm});
            skArc(sketch, "E318.MirrorCS", {"start": v(17.5, -44.19) * mm, "mid": v(15.1, -45.14) * mm, "end": v(12.52, -45.43) * mm});
            skPoint(sketch, "E319.MirrorCS.end.orphan", {"position": v(31.4, -2.9) * mm});
            skPoint(sketch, "E319.MirrorCS.start.orphan", {"position": v(31.18, -5.25) * mm});
            skArc(sketch, "E320.0", {"start": v(22.48, -1.44) * mm, "mid": v(27.1, -2.06) * mm, "end": v(31.65, -2.95) * mm});
            skArc(sketch, "E321.0", {"start": v(22.24, -3.78) * mm, "mid": v(26.96, -4.42) * mm, "end": v(31.62, -5.35) * mm});
            skArc(sketch, "E322.0", {"start": v(31.65, -2.95) * mm, "mid": v(31.65, -4.15) * mm, "end": v(31.62, -5.35) * mm});
            skPoint(sketch, "E323.MirrorCS.end.orphan", {"position": v(20.4, -45.4) * mm});
            skPoint(sketch, "E323.MirrorCS.start.orphan", {"position": v(21.77, -42.45) * mm});
            skArc(sketch, "E324.0", {"start": v(24.52, -44.28) * mm, "mid": v(24.93, -43.04) * mm, "end": v(25.32, -41.8) * mm});
            skArc(sketch, "E325.0", {"start": v(17.5, -44.19) * mm, "mid": v(20.44, -42.86) * mm, "end": v(23.57, -42.06) * mm});
            skArc(sketch, "E326.0", {"start": v(18.64, -46.24) * mm, "mid": v(21.22, -45.08) * mm, "end": v(23.96, -44.37) * mm});
            skArc(sketch, "E327.0", {"start": v(23.57, -42.06) * mm, "mid": v(24.45, -41.92) * mm, "end": v(25.32, -41.8) * mm});
            skArc(sketch, "E328.0", {"start": v(23.96, -44.37) * mm, "mid": v(24.24, -44.33) * mm, "end": v(24.52, -44.28) * mm});
            skArc(sketch, "E329.MirrorCS", {"start": v(-12.84, -28.86) * mm, "mid": v(-12.25, -29.12) * mm, "end": v(-11.63, -29.31) * mm});
            skArc(sketch, "E330.MirrorCS", {"start": v(-23.96, -44.37) * mm, "mid": v(-24.24, -44.33) * mm, "end": v(-24.52, -44.28) * mm});
            skArc(sketch, "E331.MirrorCS", {"start": v(-31.65, -2.95) * mm, "mid": v(-31.65, -4.15) * mm, "end": v(-31.62, -5.35) * mm});
            skArc(sketch, "E332.MirrorCS", {"start": v(-12.6, -26.44) * mm, "mid": v(-11.93, -26.77) * mm, "end": v(-11.21, -27) * mm});
            skArc(sketch, "E333.MirrorCS", {"start": v(-23.57, -42.06) * mm, "mid": v(-24.45, -41.92) * mm, "end": v(-25.32, -41.8) * mm});
            skArc(sketch, "E334.MirrorCS", {"start": v(-24.52, -44.28) * mm, "mid": v(-24.93, -43.04) * mm, "end": v(-25.32, -41.8) * mm});
            skArc(sketch, "E335.MirrorCS", {"start": v(-17.82, -13.22) * mm, "mid": v(-18.05, -13.52) * mm, "end": v(-18.26, -13.83) * mm});
            skArc(sketch, "E336.MirrorCS", {"start": v(-15.91, -14.6) * mm, "mid": v(-16.55, -15.63) * mm, "end": v(-16.93, -16.78) * mm});
            skPoint(sketch, "E337.MirrorP", {"position": v(-31.18, -5.25) * mm});
            skArc(sketch, "E338.MirrorCS", {"start": v(-17.5, -44.19) * mm, "mid": v(-20.44, -42.86) * mm, "end": v(-23.57, -42.06) * mm});
            skPoint(sketch, "E339.MirrorP", {"position": v(-31.4, -2.9) * mm});
            skPoint(sketch, "E340.MirrorP", {"position": v(-20.4, -45.4) * mm});
            skArc(sketch, "E341.MirrorCS", {"start": v(-18.64, -46.24) * mm, "mid": v(-21.22, -45.08) * mm, "end": v(-23.96, -44.37) * mm});
            skPoint(sketch, "E342.MirrorP", {"position": v(-21.77, -42.45) * mm});
            skArc(sketch, "E343.MirrorCS", {"start": v(-7.36, -29.74) * mm, "mid": v(-9.02, -28) * mm, "end": v(-11.21, -27) * mm});
            skArc(sketch, "E344.MirrorCS", {"start": v(-16.93, -16.78) * mm, "mid": v(-16.3, -22.3) * mm, "end": v(-12.6, -26.44) * mm});
            skPoint(sketch, "E345.MirrorP", {"position": v(-9.56, -27.1) * mm});
            skArc(sketch, "E346.MirrorCS", {"start": v(-19.44, -17.21) * mm, "mid": v(-17.94, -24.06) * mm, "end": v(-12.84, -28.86) * mm});
            skArc(sketch, "E347.MirrorCS", {"start": v(-22.48, -1.44) * mm, "mid": v(-27.1, -2.06) * mm, "end": v(-31.65, -2.95) * mm});
            skArc(sketch, "E348.MirrorCS", {"start": v(-12.52, -45.43) * mm, "mid": v(-10.76, -44.96) * mm, "end": v(-9.42, -43.73) * mm});
            skArc(sketch, "E349.MirrorCS", {"start": v(-22.24, -3.78) * mm, "mid": v(-26.96, -4.42) * mm, "end": v(-31.62, -5.35) * mm});
            skPoint(sketch, "E350.MirrorP", {"position": v(-11.7, -26.9) * mm});
            skArc(sketch, "E351.MirrorCS", {"start": v(-18.26, -13.83) * mm, "mid": v(-19.04, -15.46) * mm, "end": v(-19.44, -17.21) * mm});
            skArc(sketch, "E352.MirrorCS", {"start": v(-15.91, -14.6) * mm, "mid": v(-14.96, -5.96) * mm, "end": v(-22.37, -1.43) * mm});
            skArc(sketch, "E353.MirrorCS", {"start": v(-17.82, -13.22) * mm, "mid": v(-17.02, -7.1) * mm, "end": v(-22.23, -3.78) * mm});
            skArc(sketch, "E354.MirrorCS", {"start": v(-18.64, -46.24) * mm, "mid": v(-15.77, -47.4) * mm, "end": v(-12.7, -47.78) * mm});
            skArc(sketch, "E355.MirrorCS", {"start": v(-9.4, -30.9) * mm, "mid": v(-10.37, -29.9) * mm, "end": v(-11.63, -29.31) * mm});
            skArc(sketch, "E356.MirrorCS", {"start": v(-7.95, -45.73) * mm, "mid": v(-5.14, -37.83) * mm, "end": v(-7.36, -29.74) * mm});
            skArc(sketch, "E357.MirrorCS", {"start": v(-9.42, -43.73) * mm, "mid": v(-7.48, -37.32) * mm, "end": v(-9.4, -30.9) * mm});
            skArc(sketch, "E358.MirrorCS", {"start": v(-12.7, -47.78) * mm, "mid": v(-10.11, -47.25) * mm, "end": v(-7.95, -45.73) * mm});
            skPoint(sketch, "E359.MirrorP", {"position": v(-12, -29.24) * mm});
            skArc(sketch, "E360.MirrorCS", {"start": v(-17.5, -44.19) * mm, "mid": v(-15.1, -45.14) * mm, "end": v(-12.52, -45.43) * mm});
            skArc(sketch, "E361", {"start": v(22.48, -1.44) * mm, "mid": v(22.43, -1.43) * mm, "end": v(22.37, -1.43) * mm});
            skArc(sketch, "E362", {"start": v(22.24, -3.78) * mm, "mid": v(22.24, -3.78) * mm, "end": v(22.23, -3.78) * mm});
            skArc(sketch, "E363.MirrorCS", {"start": v(-22.48, -1.44) * mm, "mid": v(-22.43, -1.43) * mm, "end": v(-22.37, -1.43) * mm});
            skArc(sketch, "E364.MirrorCS", {"start": v(-22.24, -3.78) * mm, "mid": v(-22.24, -3.78) * mm, "end": v(-22.23, -3.78) * mm});
            skSolve(sketch);
        }
        {
            var Q0;
            Q0=qSketchRegion(id+"F9",true);
            extrude(context, id + "F10", {"entities" : qUnion([Q0]), "operationType" : NewBodyOperationType.ADD, "depth" : 6.35 * mm});
        }
        {
            var Q0;
            Q0=qCreatedBy(makeId("Top.planeOp"),FACE);
            var sketch = newSketch(context, id + "F11", { "sketchPlane" : qUnion([Q0])});
            skLineSegment(sketch, "E365", {"start": v(91.05, 0) * mm, "end": v(-86.67, 0) * mm, "construction": true});
            skLineSegment(sketch, "E366", {"start": v(0, 79.99) * mm, "end": v(0, -101.6) * mm, "construction": true});
            skPoint(sketch, "E367", {"position": v(0, 0) * mm});
            skPoint(sketch, "E368", {"position": v(-22.23, 0) * mm});
            skPoint(sketch, "E369", {"position": v(22.23, 0) * mm});
            skPoint(sketch, "E370", {"position": v(0, 44.45) * mm});
            skPoint(sketch, "E371", {"position": v(-11.43, 76.2) * mm});
            skPoint(sketch, "E372", {"position": v(11.43, 76.2) * mm});
            skPoint(sketch, "E373", {"position": v(-6.35, 50.8) * mm});
            skPoint(sketch, "E374", {"position": v(6.35, 50.8) * mm});
            skLineSegment(sketch, "E375", {"start": v(-6.35, 44.45) * mm, "end": v(6.35, 44.45) * mm, "construction": true});
            skArc(sketch, "E376", {"start": v(-1.54, 44.64) * mm, "mid": v(0, 44.45) * mm, "end": v(1.54, 44.64) * mm});
            skLineSegment(sketch, "E377", {"start": v(-6.35, 44.45) * mm, "end": v(0, 50.8) * mm, "construction": true});
            skLineSegment(sketch, "E378", {"start": v(0, 50.8) * mm, "end": v(6.35, 44.45) * mm, "construction": true});
            skPoint(sketch, "E379", {"position": v(-4.5, 46.3) * mm});
            skPoint(sketch, "E380", {"position": v(4.5, 46.3) * mm});
            skArc(sketch, "E381", {"start": v(-11.43, 76.2) * mm, "mid": v(-9.27, 61.75) * mm, "end": v(-5.06, 47.76) * mm});
            skArc(sketch, "E382", {"start": v(5.06, 47.76) * mm, "mid": v(9.27, 61.75) * mm, "end": v(11.43, 76.2) * mm});
            skArc(sketch, "E383.filletArc", {"start": v(-5.06, 47.76) * mm, "mid": v(-3.68, 45.77) * mm, "end": v(-1.54, 44.64) * mm});
            skArc(sketch, "E384.filletArc", {"start": v(1.54, 44.64) * mm, "mid": v(3.68, 45.77) * mm, "end": v(5.06, 47.76) * mm});
            skLineSegment(sketch, "E385", {"start": v(19.05, -57.15) * mm, "end": v(-20.16, -57.15) * mm, "construction": true});
            skLineSegment(sketch, "E386", {"start": v(16.51, -19.05) * mm, "end": v(-17.62, -19.05) * mm, "construction": true});
            skArc(sketch, "E387", {"start": v(-11.43, 76.2) * mm, "mid": v(-20.39, 28.96) * mm, "end": v(-17.62, -19.05) * mm});
            skArc(sketch, "E388", {"start": v(16.51, -19.05) * mm, "mid": v(19.83, 28.89) * mm, "end": v(11.43, 76.2) * mm});
            skArc(sketch, "E389", {"start": v(-19.1, -50.97) * mm, "mid": v(-17.52, -35.05) * mm, "end": v(-17.62, -19.05) * mm});
            skArc(sketch, "E390", {"start": v(16.51, -19.05) * mm, "mid": v(16.39, -34.66) * mm, "end": v(17.86, -50.2) * mm});
            skLineSegment(sketch, "E391", {"start": v(0, -101.6) * mm, "end": v(27.94, -101.6) * mm, "construction": true});
            skLineSegment(sketch, "E392", {"start": v(0, -101.6) * mm, "end": v(-27.94, -101.6) * mm, "construction": true});
            skArc(sketch, "E393", {"start": v(-21.7, -61.04) * mm, "mid": v(-26.64, -79.48) * mm, "end": v(-28.05, -98.52) * mm});
            skArc(sketch, "E394", {"start": v(27.98, -98.33) * mm, "mid": v(26.14, -79.57) * mm, "end": v(20.88, -61.48) * mm});
            skPoint(sketch, "E395", {"position": v(0, -60.96) * mm});
            skArc(sketch, "E396", {"start": v(0, -60.96) * mm, "mid": v(-15.6, -78.3) * mm, "end": v(-26.83, -98.75) * mm});
            skArc(sketch, "E397", {"start": v(26.76, -98.57) * mm, "mid": v(15.54, -78.23) * mm, "end": v(0, -60.96) * mm});
            skPoint(sketch, "E398.visualSharp", {"position": v(-20.16, -57.15) * mm});
            skArc(sketch, "E398.filletArc", {"start": v(-21.7, -61.04) * mm, "mid": v(-20.14, -56.07) * mm, "end": v(-19.1, -50.97) * mm});
            skPoint(sketch, "E399.visualSharp", {"position": v(19.05, -57.15) * mm});
            skArc(sketch, "E399.filletArc", {"start": v(17.86, -50.2) * mm, "mid": v(19.05, -55.93) * mm, "end": v(20.88, -61.48) * mm});
            skPoint(sketch, "E400.visualSharp", {"position": v(-27.94, -101.6) * mm});
            skArc(sketch, "E400.filletArc", {"start": v(-28.05, -98.52) * mm, "mid": v(-27.53, -99.13) * mm, "end": v(-26.83, -98.75) * mm});
            skPoint(sketch, "E401.visualSharp", {"position": v(27.94, -101.6) * mm});
            skArc(sketch, "E401.filletArc", {"start": v(26.76, -98.57) * mm, "mid": v(27.47, -98.95) * mm, "end": v(27.98, -98.33) * mm});
            skPoint(sketch, "E402", {"position": v(15.24, 0) * mm});
            skCircle(sketch, "E403", {"center": v(15.24, 0) * mm, "radius": 1.59 * mm});
            skCircle(sketch, "E404", {"center": v(15.24, 0) * mm, "radius": 3.18 * mm, "construction": true});
            skPoint(sketch, "E405.MirrorP", {"position": v(-15.24, 0) * mm});
            skCircle(sketch, "E406.MirrorC", {"center": v(-15.24, 0) * mm, "radius": 1.59 * mm});
            skCircle(sketch, "E407.MirrorC", {"center": v(-15.24, 0) * mm, "radius": 3.18 * mm, "construction": true});
            skCircle(sketch, "E408.MirrorC", {"center": v(-11.43, 51.44) * mm, "radius": 1.59 * mm});
            skCircle(sketch, "E409.MirrorC", {"center": v(-11.43, 51.44) * mm, "radius": 3.18 * mm, "construction": true});
            skCircle(sketch, "E410.MirrorC", {"center": v(11.43, 51.44) * mm, "radius": 3.18 * mm, "construction": true});
            skCircle(sketch, "E411.MirrorC", {"center": v(11.43, 51.44) * mm, "radius": 1.59 * mm});
            skCircle(sketch, "E412.MirrorC", {"center": v(-11.43, -62.23) * mm, "radius": 1.59 * mm});
            skCircle(sketch, "E413.MirrorC", {"center": v(-11.43, -62.23) * mm, "radius": 3.18 * mm, "construction": true});
            skCircle(sketch, "E414.MirrorC", {"center": v(11.43, -62.23) * mm, "radius": 3.18 * mm, "construction": true});
            skCircle(sketch, "E415.MirrorC", {"center": v(11.43, -62.23) * mm, "radius": 1.59 * mm});
            skSolve(sketch);
        }
        {
            var Q0;
            Q0=makeQuery(id+"F11.imprint","IMPRINT",FACE,{"disambiguationData":[TD([[makeQuery(id+"F11.imprint","IMPRINT",EDGE,{"derivedFrom":sQuery(id+"F11.wireOp",EDGE,"E412.MirrorC")}),-1.0]])]});
            var Q1;
            Q1=makeQuery(id+"F11.imprint","IMPRINT",FACE,{"disambiguationData":[TD([[makeQuery(id+"F11.imprint","IMPRINT",EDGE,{"derivedFrom":sQuery(id+"F11.wireOp",EDGE,"E411.MirrorC")}),1.0]])]});
            var Q2;
            Q2=makeQuery(id+"F11.imprint","IMPRINT",FACE,{"disambiguationData":[TD([[makeQuery(id+"F11.imprint","IMPRINT",EDGE,{"derivedFrom":sQuery(id+"F11.wireOp",EDGE,"E408.MirrorC")}),-1.0]])]});
            var Q3;
            Q3=makeQuery(id+"F11.imprint","IMPRINT",FACE,{"disambiguationData":[TD([[makeQuery(id+"F11.imprint","IMPRINT",EDGE,{"derivedFrom":sQuery(id+"F11.wireOp",EDGE,"E406.MirrorC")}),-1.0]])]});
            var Q4;
            Q4=makeQuery(id+"F11.imprint","IMPRINT",FACE,{"disambiguationData":[TD([[makeQuery(id+"F11.imprint","IMPRINT",EDGE,{"derivedFrom":sQuery(id+"F11.wireOp",EDGE,"E403")}),1.0]])]});
            var Q5;
            Q5=makeQuery(id+"F11.imprint","IMPRINT",FACE,{"disambiguationData":[TD([[makeQuery(id+"F11.imprint","IMPRINT",EDGE,{"derivedFrom":sQuery(id+"F11.wireOp",EDGE,"E415.MirrorC")}),1.0]])]});
            extrude(context, id + "F12", {"entities" : qUnion([Q0, Q1, Q2, Q3, Q4, Q5]), "operationType" : NewBodyOperationType.REMOVE, "oppositeDirection" : true, "depth" : 25.4 * mm});
        }
        {
            var Q0;
            Q0=makeQuery(id+"F10.opExtrude","CAP_EDGE",EDGE,{"disambiguationData":[OSD([sQuery(id+"F9.wireOp",EDGE,"E291.MirrorCS")])],"isStart":false});
            var Q1;
            Q1=makeQuery(id+"F10.opExtrude","CAP_EDGE",EDGE,{"disambiguationData":[OSD([sQuery(id+"F9.wireOp",EDGE,"E292.MirrorCS")])],"isStart":false});
            var Q2;
            Q2=makeQuery(id+"F10.opExtrude","CAP_EDGE",EDGE,{"disambiguationData":[OSD([sQuery(id+"F9.wireOp",EDGE,"E294.MirrorCS")])],"isStart":false});
            var Q3;
            Q3=makeQuery(id+"F10.opExtrude","CAP_EDGE",EDGE,{"disambiguationData":[OSD([sQuery(id+"F9.wireOp",EDGE,"E275.MirrorCS")])],"isStart":false});
            var Q4;
            Q4=makeQuery(id+"F10.opExtrude","CAP_EDGE",EDGE,{"disambiguationData":[OSD([sQuery(id+"F9.wireOp",EDGE,"E298.MirrorCS")])],"isStart":false});
            var Q5;
            Q5=makeQuery(id+"F10.opExtrude","CAP_EDGE",EDGE,{"disambiguationData":[OSD([sQuery(id+"F9.wireOp",EDGE,"E278.MirrorCS")])],"isStart":false});
            var Q6;
            Q6=makeQuery(id+"F10.opExtrude","CAP_EDGE",EDGE,{"disambiguationData":[OSD([sQuery(id+"F9.wireOp",EDGE,"E283.MirrorCS")])],"isStart":false});
            var Q7;
            Q7=makeQuery(id+"F10.opExtrude","CAP_EDGE",EDGE,{"disambiguationData":[OSD([sQuery(id+"F9.wireOp",EDGE,"E295.MirrorCS")])],"isStart":false});
            var Q8;
            Q8=makeQuery(id+"F10.opExtrude","CAP_EDGE",EDGE,{"disambiguationData":[OSD([sQuery(id+"F9.wireOp",EDGE,"E277.MirrorCS")])],"isStart":false});
            var Q9;
            Q9=makeQuery(id+"F10.opExtrude","CAP_EDGE",EDGE,{"disambiguationData":[OSD([sQuery(id+"F9.wireOp",EDGE,"E287.MirrorCS")])],"isStart":false});
            var Q10;
            Q10=makeQuery(id+"F10.opExtrude","CAP_EDGE",EDGE,{"disambiguationData":[OSD([sQuery(id+"F9.wireOp",EDGE,"E284.MirrorCS")])],"isStart":false});
            var Q11;
            Q11=makeQuery(id+"F10.opExtrude","CAP_EDGE",EDGE,{"disambiguationData":[OSD([sQuery(id+"F9.wireOp",EDGE,"E285.MirrorCS")])],"isStart":false});
            var Q12;
            Q12=makeQuery(id+"F10.opExtrude","CAP_EDGE",EDGE,{"disambiguationData":[OSD([sQuery(id+"F9.wireOp",EDGE,"E280.MirrorCS")])],"isStart":false});
            var Q13;
            Q13=makeQuery(id+"F10.opExtrude","CAP_EDGE",EDGE,{"disambiguationData":[OSD([sQuery(id+"F9.wireOp",EDGE,"E276.MirrorCS")])],"isStart":false});
            fillet(context, id + "F13", {"entities" : qUnion([Q0, Q1, Q2, Q3, Q4, Q5, Q6, Q7, Q8, Q9, Q10, Q11, Q12, Q13]), "radius" : 0.92 * mm, "tangentPropagation" : true, "allowEdgeOverflow" : false});
        }
        {
            var Q0;
            Q0=makeQuery(id+"F10.opExtrude","SWEPT_EDGE",EDGE,{"disambiguationData":[OSD([sQuery(id+"F9.wireOp",EDGE,"E280.MirrorCS"),sQuery(id+"F9.wireOp",EDGE,"E296.MirrorCS")])]});
            fillet(context, id + "F14", {"entities" : qUnion([Q0]), "radius" : 0.64 * mm, "tangentPropagation" : true, "allowEdgeOverflow" : false});
        }
    });
